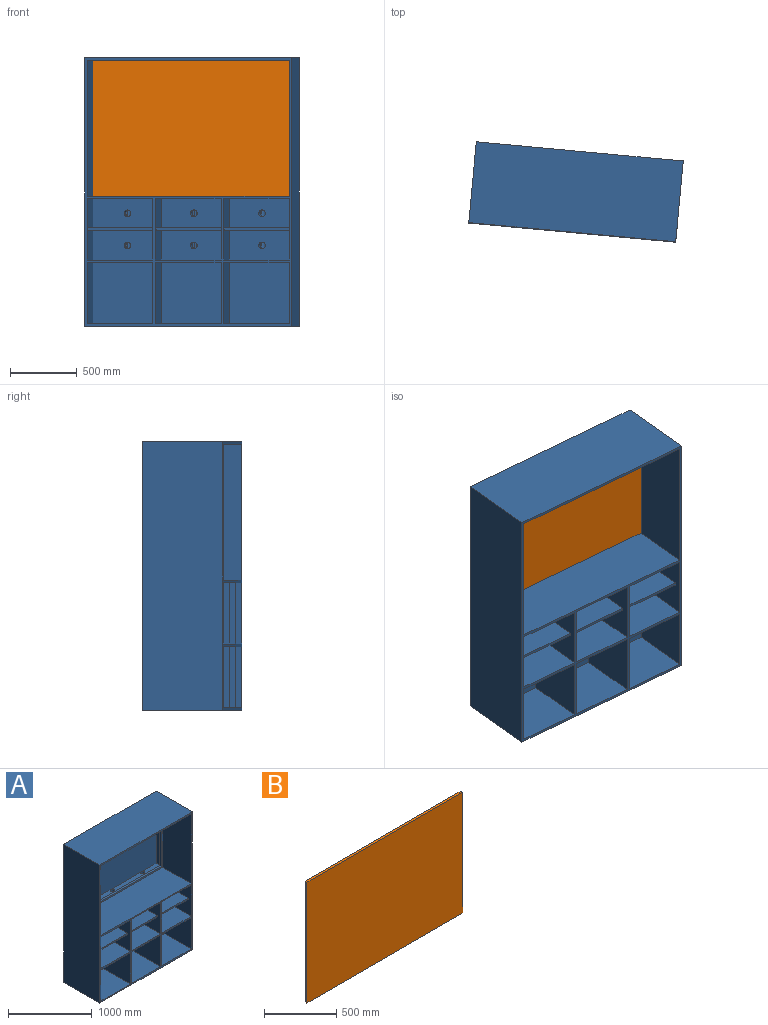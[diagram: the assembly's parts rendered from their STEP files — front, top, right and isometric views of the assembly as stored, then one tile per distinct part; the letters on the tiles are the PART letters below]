
ASSEMBLY  parts=2 mates=1
PART A: 98 faces, bbox 1562.1x609.6x2019.3 mm
  f0: plane 1524x476.25mm, normal (0,0,-1), area 725805mm2, adj f4,f6,f16,f94
  f1: plane 971.55x25.4mm, normal (1,0,0), area 24677.4mm2, adj f94,f95,f96,f97
  f2: plane 1524x476.25mm, normal (0,0,1), area 725805mm2, adj f4,f6,f16,f94
  f3: plane 971.55x25.4mm, normal (-1,0,0), area 24677.4mm2, adj f94,f95,f96,f97
  f4: plane 1022.35x476.25mm, normal (-1,0,0), area 486894.2mm2, adj f0,f2,f16,f94
  f5: plane 1524x90.81mm, normal (0,0,-1), area 138386.8mm2, adj f61,f62,f63,f95
  f6: plane 1022.35x476.25mm, normal (1,0,0), area 486894.2mm2, adj f0,f2,f16,f94
  f7: plane 1524x90.81mm, normal (0,0,1), area 132341.3mm2, adj f61,f62,f63,f67,f71,f76,f95
  f8: cylinder r=25.4mm len=133.35mm, axis (0,-1,0), area 15858.5mm2, adj f9,f60,f76
  f9: plane 42.33x11.35mm, normal (0,-1,0), area 338.2mm2, adj f8,f76
  f10: cylinder r=25.4mm len=109.86mm, axis (0,-1,0), area 14951.4mm2, adj f55,f67
  f11: cylinder r=25.4mm len=109.86mm, axis (0,-1,0), area 14951.4mm2, adj f50,f71
  f12: cylinder r=25.4mm len=133.35mm, axis (0,-1,0), area 15858.5mm2, adj f13,f45,f76
  f13: plane 42.33x11.35mm, normal (0,-1,0), area 338.2mm2, adj f12,f76
  f14: cylinder r=25.4mm len=109.86mm, axis (0,-1,0), area 14951.4mm2, adj f27,f71
  f15: cylinder r=25.4mm len=109.86mm, axis (0,-1,0), area 14951.4mm2, adj f24,f67
  f16: plane 2019.3x1562.1mm, normal (0,-1,0), area 228144.7mm2, adj f0,f2,f4,f6,f17,f18,f19,f20
  f17: plane 1562.1x609.6mm, normal (0,0,1), area 952256.2mm2, adj f16,f18,f20,f21
  f18: plane 2019.3x609.6mm, normal (-1,0,0), area 1230965.3mm2, adj f16,f17,f19,f21
  f19: plane 1562.1x609.6mm, normal (0,0,-1), area 952256.2mm2, adj f16,f18,f20,f21
  f20: plane 2019.3x609.6mm, normal (1,0,0), area 1230965.3mm2, adj f16,f17,f19,f21
  f21: plane 2019.3x1562.1mm, normal (0,1,0), area 3154348.5mm2, adj f17,f18,f19,f20
  f22: plane 495.3x406.4mm, normal (0,0,-1), area 201289.9mm2, adj f24,f51,f53,f65
  f23: plane 495.3x457.2mm, normal (0,0,1), area 226451.2mm2, adj f16,f24,f51,f53
  f24: plane 495.3x222.25mm, normal (0,-1,0), area 108053.6mm2, adj f15,f22,f23,f51,f53
  f25: plane 495.3x457.2mm, normal (0,0,-1), area 226451.2mm2, adj f16,f27,f46,f48
  f26: plane 495.3x406.4mm, normal (0,0,1), area 201289.9mm2, adj f27,f46,f48,f66
  f27: plane 495.3x219.08mm, normal (0,-1,0), area 106481mm2, adj f14,f25,f26,f46,f48
  f28: plane 495.3x457.2mm, normal (0,0,1), area 226451.2mm2, adj f16,f29,f31,f32
  f29: plane 460.38x457.2mm, normal (-1,0,0), area 210483.4mm2, adj f16,f28,f30,f32
  f30: plane 495.3x457.2mm, normal (0,0,-1), area 226451.2mm2, adj f16,f29,f31,f32
  f31: plane 460.38x457.2mm, normal (1,0,0), area 210483.4mm2, adj f16,f28,f30,f32
  f32: plane 495.3x460.38mm, normal (0,-1,0), area 228023.7mm2, adj f28,f29,f30,f31
  f33: plane 460.38x457.2mm, normal (-1,0,0), area 210483.4mm2, adj f16,f34,f36,f37
  f34: plane 495.3x457.2mm, normal (0,0,-1), area 226451.2mm2, adj f16,f33,f35,f37
  f35: plane 460.38x457.2mm, normal (1,0,0), area 210483.4mm2, adj f16,f34,f36,f37
  f36: plane 495.3x457.2mm, normal (0,0,1), area 226451.2mm2, adj f16,f33,f35,f37
  f37: plane 495.3x460.38mm, normal (0,-1,0), area 228023.7mm2, adj f33,f34,f35,f36
  f38: plane 460.38x457.2mm, normal (-1,0,0), area 210483.4mm2, adj f16,f39,f41,f42
  f39: plane 495.3x457.2mm, normal (0,0,-1), area 226451.2mm2, adj f16,f38,f40,f42
  f40: plane 460.38x457.2mm, normal (1,0,0), area 210483.4mm2, adj f16,f39,f41,f42
  f41: plane 495.3x457.2mm, normal (0,0,1), area 226451.2mm2, adj f16,f38,f40,f42
  f42: plane 495.3x460.38mm, normal (0,-1,0), area 228023.7mm2, adj f38,f39,f40,f41
  f43: plane 495.3x457.2mm, normal (0,0,-1), area 226451.2mm2, adj f16,f45,f57,f59
  f44: plane 495.3x406.4mm, normal (0,0,1), area 201289.9mm2, adj f45,f57,f59,f64
  f45: plane 495.3x219.08mm, normal (0,-1,0), area 106481mm2, adj f12,f43,f44,f57,f59
  f46: plane 460.38x457.2mm, normal (-1,0,0), area 202741.5mm2, adj f16,f25,f26,f27,f47,f49,f50,f66
  f47: plane 495.3x406.4mm, normal (0,0,-1), area 201289.9mm2, adj f46,f48,f50,f66
  f48: plane 460.38x457.2mm, normal (1,0,0), area 202741.5mm2, adj f16,f25,f26,f27,f47,f49,f50,f66
  f49: plane 495.3x457.2mm, normal (0,0,1), area 226451.2mm2, adj f16,f46,f48,f50
  f50: plane 495.3x222.25mm, normal (0,-1,0), area 108053.6mm2, adj f11,f46,f47,f48,f49
  f51: plane 460.38x457.2mm, normal (-1,0,0), area 202741.5mm2, adj f16,f22,f23,f24,f52,f54,f55,f65
  f52: plane 495.3x457.2mm, normal (0,0,-1), area 226451.2mm2, adj f16,f51,f53,f55
  f53: plane 460.38x457.2mm, normal (1,0,0), area 202741.5mm2, adj f16,f22,f23,f24,f52,f54,f55,f65
  f54: plane 495.3x406.4mm, normal (0,0,1), area 201289.9mm2, adj f51,f53,f55,f65
  f55: plane 495.3x219.08mm, normal (0,-1,0), area 106481mm2, adj f10,f51,f52,f53,f54
  f56: plane 495.3x406.4mm, normal (0,0,-1), area 201289.9mm2, adj f57,f59,f60,f64
  f57: plane 460.38x457.2mm, normal (1,0,0), area 202741.5mm2, adj f16,f43,f44,f45,f56,f58,f60,f64
  f58: plane 495.3x457.2mm, normal (0,0,1), area 226451.2mm2, adj f16,f57,f59,f60
  f59: plane 460.38x457.2mm, normal (-1,0,0), area 202741.5mm2, adj f16,f43,f44,f45,f56,f58,f60,f64
  f60: plane 495.3x222.25mm, normal (0,-1,0), area 108053.6mm2, adj f8,f56,f57,f58,f59
  f61: plane 1022.35x90.81mm, normal (-1,0,0), area 92834.5mm2, adj f5,f7,f63,f95
  f62: plane 1022.35x90.81mm, normal (1,0,0), area 92834.5mm2, adj f5,f7,f63,f95
  f63: plane 1524x1022.35mm, normal (0,-1,0), area 1558061.4mm2, adj f5,f7,f61,f62,f75
  f64: plane 495.3x19.05mm, normal (0,-1,0), area 9435.5mm2, adj f44,f56,f57,f59
  f65: plane 495.3x19.05mm, normal (0,-1,0), area 9435.5mm2, adj f22,f51,f53,f54
  f66: plane 495.3x19.05mm, normal (0,-1,0), area 9435.5mm2, adj f26,f46,f47,f48
  f67: cylinder r=25.4mm len=425.45mm, axis (0,0,1), area 59537.4mm2, adj f7,f10,f15,f68,f69,f70,f84,f85
  f68: cone r=0mm half-angle=59deg, axis (0,0,1), area 2364.6mm2, adj f67
  f69: plane 46.99x15.75mm, normal (0,-1,0), area 535.2mm2, adj f67,f70
  f70: cylinder r=25.4mm len=46.99mm, axis (0,-1,0), area 609.6mm2, adj f67,f69
  f71: cylinder r=25.4mm len=425.45mm, axis (0,0,1), area 59537.4mm2, adj f7,f11,f14,f72,f73,f74,f80,f81
  f72: cone r=0mm half-angle=59deg, axis (0,0,1), area 2364.6mm2, adj f71
  f73: plane 46.99x15.75mm, normal (0,-1,0), area 535.2mm2, adj f71,f74
  f74: cylinder r=25.4mm len=46.99mm, axis (0,-1,0), area 609.6mm2, adj f71,f73
  f75: plane 21.59x2.41mm, normal (0,0,-1), area 35mm2, adj f63,f76
  f76: cylinder r=25.4mm len=425.45mm, axis (0,0,1), area 60486.2mm2, adj f7,f8,f9,f12,f13,f75,f77,f78
  f77: cone r=0mm half-angle=59deg, axis (0,0,1), area 2364.6mm2, adj f76
  f78: plane 42.02x11.13mm, normal (0,-1,0), area 328.5mm2, adj f76,f79
  f79: cylinder r=25.4mm len=42.02mm, axis (0,-1,0), area 458.7mm2, adj f76,f78
  f80: plane 46.99x15.75mm, normal (0,-1,0), area 535.2mm2, adj f71,f81
  f81: cylinder r=25.4mm len=46.99mm, axis (0,-1,0), area 609.6mm2, adj f71,f80
  f82: plane 46.99x15.75mm, normal (0,-1,0), area 535.2mm2, adj f71,f83
  f83: cylinder r=25.4mm len=46.99mm, axis (0,-1,0), area 609.6mm2, adj f71,f82
  f84: plane 46.99x15.75mm, normal (0,-1,0), area 535.2mm2, adj f67,f85
  f85: cylinder r=25.4mm len=46.99mm, axis (0,-1,0), area 609.6mm2, adj f67,f84
  f86: plane 46.99x15.75mm, normal (0,-1,0), area 535.2mm2, adj f67,f87
  f87: cylinder r=25.4mm len=46.99mm, axis (0,-1,0), area 609.6mm2, adj f67,f86
  f88: plane 42.02x11.13mm, normal (0,-1,0), area 328.5mm2, adj f76,f89
  f89: cylinder r=25.4mm len=42.02mm, axis (0,-1,0), area 458.7mm2, adj f76,f88
  f90: plane 46.99x15.75mm, normal (0,-1,0), area 535.2mm2, adj f67,f91
  f91: cylinder r=25.4mm len=46.99mm, axis (0,-1,0), area 609.6mm2, adj f67,f90
  f92: plane 46.99x15.75mm, normal (0,-1,0), area 535.2mm2, adj f71,f93
  f93: cylinder r=25.4mm len=46.99mm, axis (0,-1,0), area 609.6mm2, adj f71,f92
  f94: plane 1524x1022.35mm, normal (0,-1,0), area 126773.9mm2, adj f0,f1,f2,f3,f4,f6,f96,f97
  f95: plane 1524x1022.35mm, normal (0,1,0), area 126773.9mm2, adj f1,f3,f5,f7,f61,f62,f96,f97
  f96: plane 1473.2x25.4mm, normal (0,0,1), area 37419.3mm2, adj f1,f3,f94,f95
  f97: plane 1473.2x25.4mm, normal (0,0,-1), area 37419.3mm2, adj f1,f3,f94,f95
PART B: 6 faces, bbox 1524x19.1x1022.4 mm
  f0: plane 1022.35x19.05mm, normal (1,0,0), area 19475.8mm2, adj f1,f3,f4,f5
  f1: plane 1524x19.05mm, normal (0,0,1), area 29032.2mm2, adj f0,f2,f4,f5
  f2: plane 1022.35x19.05mm, normal (-1,0,0), area 19475.8mm2, adj f1,f3,f4,f5
  f3: plane 1524x19.05mm, normal (0,0,-1), area 29032.2mm2, adj f0,f2,f4,f5
  f4: plane 1524x1022.35mm, normal (0,-1,0), area 1558061.4mm2, adj f0,f1,f2,f3
  f5: plane 1524x1022.35mm, normal (0,1,0), area 1558061.4mm2, adj f0,f1,f2,f3
PLACE A rot(axis=(0,0,-1),5.3deg) t=(-1179.55,-382.87,-1400.35)mm
PLACE B rot(axis=(0,0,-1),5.3deg) t=(-467.29,-582.87,38.5)mm
MATE revolute A.f94 <-> B.f5  axis (-0.09,-1,0) through (-1226.03,-512.48,38.5)mm
